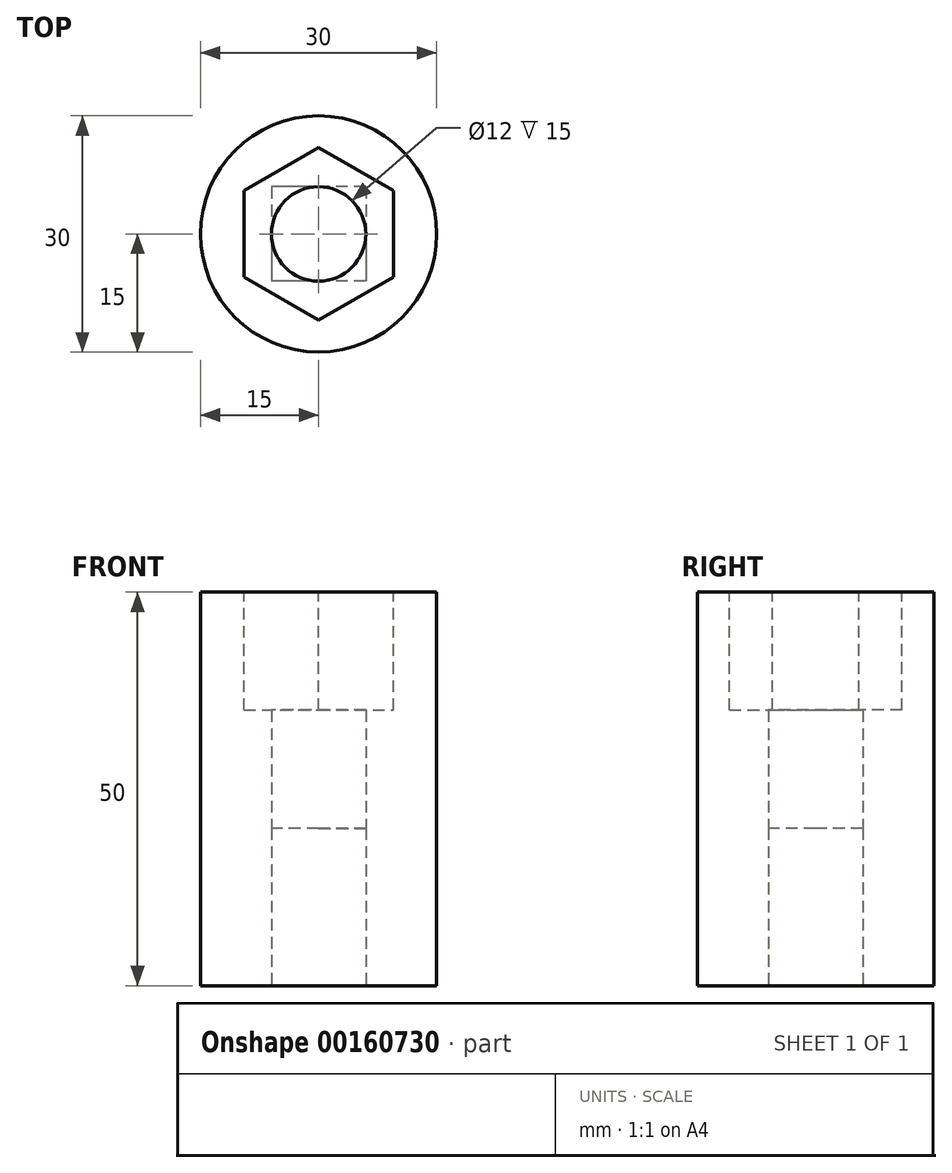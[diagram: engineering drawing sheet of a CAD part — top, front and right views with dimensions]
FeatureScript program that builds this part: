
annotation { "Feature Type Name" : "Feature", "Feature Type Description" : "" }
export const myFeature = defineFeature(function(context is Context, id is Id, definition is map)
    precondition{}
    {
        {
            var Q0;
            Q0=qCreatedBy(makeId("Top.planeOp"),FACE);
            var sketch = newSketch(context, id + "F0", { "sketchPlane" : qUnion([Q0])});
            skCircle(sketch, "E0", {"center": v(0, 0) * mm, "radius": 15 * mm});
            skSolve(sketch);
        }
        {
            var Q0;
            Q0 = qSketchRegion(id + "F0", true);
            extrude(context, id + "F1", {"entities" : qUnion([Q0]), "depth" : 50 * mm});
        }
        {
            var Q0;
            Q0=qCreatedBy(makeId("Top.planeOp"),FACE);
            var sketch = newSketch(context, id + "F2", { "sketchPlane" : qUnion([Q0])});
            skLineSegment(sketch, "E1.bottom", {"start": v(6, 6) * mm, "end": v(-6, 6) * mm});
            skLineSegment(sketch, "E1.top", {"start": v(6, -6) * mm, "end": v(-6, -6) * mm});
            skLineSegment(sketch, "E1.left", {"start": v(6, 6) * mm, "end": v(6, -6) * mm});
            skLineSegment(sketch, "E1.right", {"start": v(-6, 6) * mm, "end": v(-6, -6) * mm});
            skPoint(sketch, "E1.middle", {"position": v(0, 0) * mm});
            skCircle(sketch, "E2", {"center": v(0, 0) * mm, "radius": 6 * mm});
            skSolve(sketch);
        }
        {
            var Q0;
            {var subQ0=sQuery(id+"F2.wireOp",EDGE,"E2");var subQ1=makeQuery(id+"F2.imprint","INTERSECT",VERTEX,{"derivedFrom":[sQuery(id+"F2.wireOp",EDGE,"E1.bottom"),subQ0]});Q0=makeQuery(id+"F2.imprint","IMPRINT",FACE,{"disambiguationData":[TD([[makeQuery(id+"F2.imprint","IMPRINT",EDGE,{"disambiguationData":[TD([[subQ1,1.0]])],"derivedFrom":subQ0}),1.0]])]});}
            extrude(context, id + "F3", {"entities" : qUnion([Q0]), "operationType" : NewBodyOperationType.REMOVE, "endBound" : BoundingType.THROUGH_ALL, "depth" : 25 * mm});
        }
        {
            var Q0;
            Q0 = qSketchRegion(id + "F2", true);
            extrude(context, id + "F4", {"entities" : qUnion([Q0]), "operationType" : NewBodyOperationType.REMOVE, "depth" : 20 * mm});
        }
        {
            var Q0;
            Q0=makeQuery(id+"F1.opExtrude","CAP_FACE",FACE,{"disambiguationData":[OSD([sQuery(id+"F0.wireOp",EDGE,"E0")])],"isStart":false});
            var sketch = newSketch(context, id + "F5", { "sketchPlane" : qUnion([Q0])});
            skCircle(sketch, "E3.cCircle", {"center": v(0, 0) * mm, "radius": 9.5 * mm, "construction": true});
            skLineSegment(sketch, "E3.0", {"start": v(0, 10.97) * mm, "end": v(9.5, 5.48) * mm});
            skLineSegment(sketch, "E3.1", {"start": v(9.5, 5.48) * mm, "end": v(9.5, -5.48) * mm});
            skLineSegment(sketch, "E3.2", {"start": v(9.5, -5.48) * mm, "end": v(0, -10.97) * mm});
            skLineSegment(sketch, "E3.3", {"start": v(0, -10.97) * mm, "end": v(-9.5, -5.48) * mm});
            skLineSegment(sketch, "E3.4", {"start": v(-9.5, -5.48) * mm, "end": v(-9.5, 5.48) * mm});
            skLineSegment(sketch, "E3.5", {"start": v(-9.5, 5.48) * mm, "end": v(0, 10.97) * mm});
            skPoint(sketch, "E3.0.midPoint", {"position": v(4.75, 8.23) * mm});
            skSolve(sketch);
        }
        {
            var Q0;
            Q0 = qSketchRegion(id + "F5", true);
            extrude(context, id + "F6", {"entities" : qUnion([Q0]), "operationType" : NewBodyOperationType.REMOVE, "oppositeDirection" : true, "depth" : 15 * mm});
        }
    });
